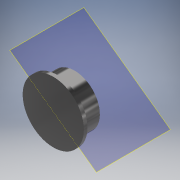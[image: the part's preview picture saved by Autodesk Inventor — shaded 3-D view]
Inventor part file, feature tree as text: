
AUTODESK INVENTOR PART (.ipt)
format: ipt  version: 2018 (Build 220112000, 112)  size: 142,336 bytes
history: native  units: in
note: dims shown in document units (in); Inventor stores cm internally (conversion verified against a paired STEP export)
features: plane x1, revolve x1, sketch x1
ambient origin geometry x8: Origin, YZ Plane, XZ Plane, XY Plane, X Axis, Y Axis, Z Axis, Center Point
bodies: Solid1 (feature_tree)
feature tree (3):
  plane  "Work Plane1"
  revolve  "Revolution1"  [1 undecoded]
  sketch  "Sketch1"  dims[d1=0.2in d4=0.1in d5=0.1in d6=0.2in d7=0.1in d8=0.1in d9=1.9144in d10=90.0deg]
note: 1 required parameter value undecoded (feature->parameter linkage not recoverable at this tier; creation-order binding heuristic only, values carry confidence <= 0.55)
